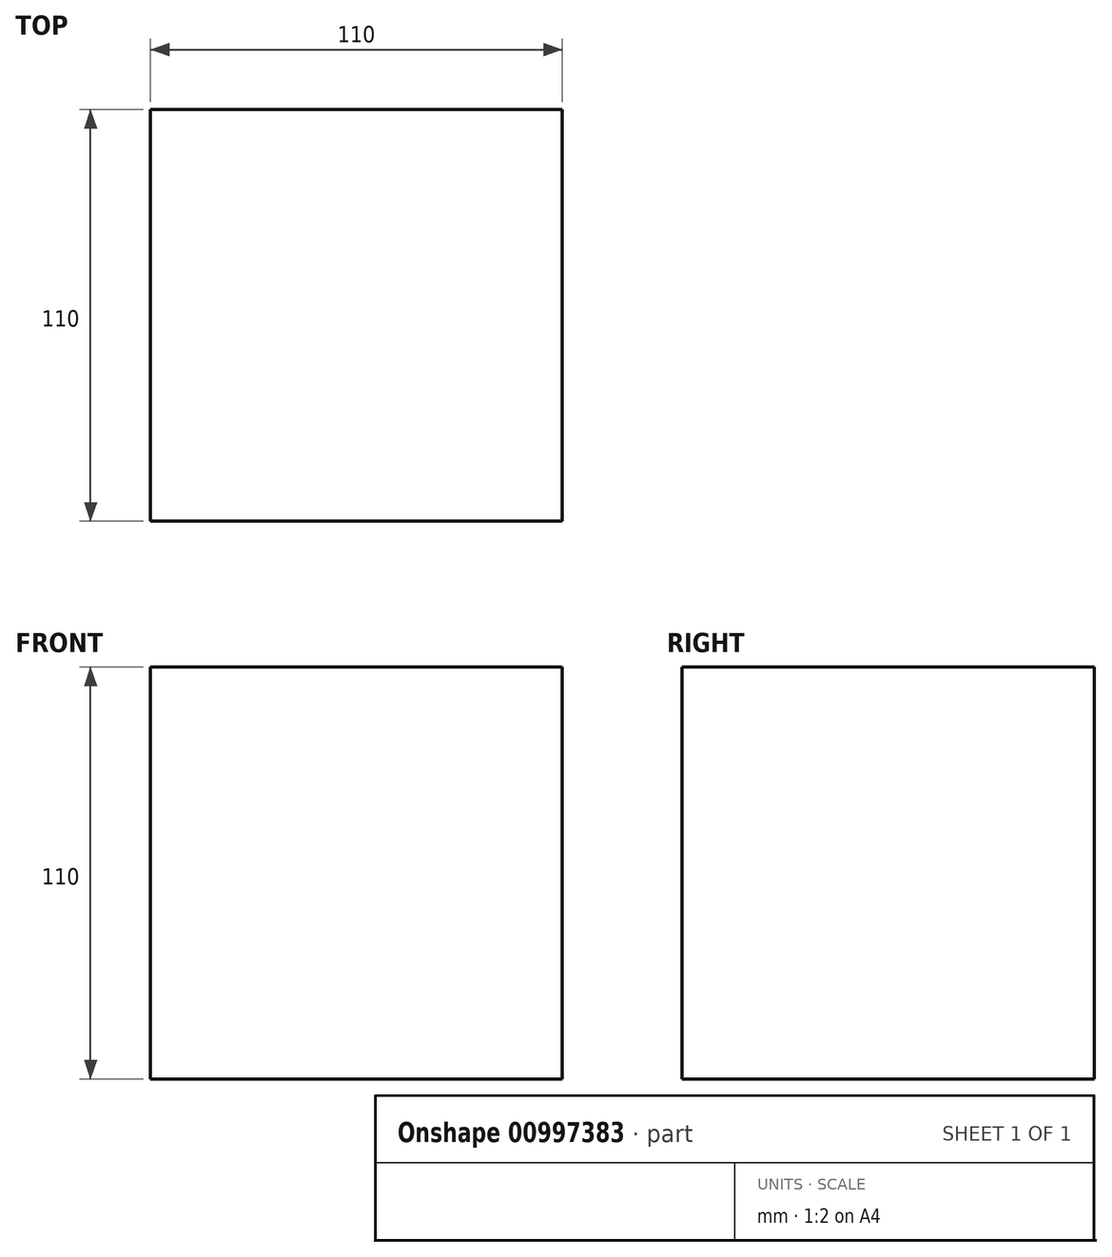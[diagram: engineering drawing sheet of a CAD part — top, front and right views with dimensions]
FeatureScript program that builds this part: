
annotation { "Feature Type Name" : "Feature", "Feature Type Description" : "" }
export const myFeature = defineFeature(function(context is Context, id is Id, definition is map)
    precondition{}
    {
        {
            var Q0;
            Q0=qCreatedBy(makeId("Front.planeOp"),FACE);
            var sketch = newSketch(context, id + "F0", { "sketchPlane" : qUnion([Q0])});
            skLineSegment(sketch, "E0.bottom", {"start": v(55, 55) * mm, "end": v(-55, 55) * mm});
            skLineSegment(sketch, "E0.top", {"start": v(55, -55) * mm, "end": v(-55, -55) * mm});
            skLineSegment(sketch, "E0.left", {"start": v(55, 55) * mm, "end": v(55, -55) * mm});
            skLineSegment(sketch, "E0.right", {"start": v(-55, 55) * mm, "end": v(-55, -55) * mm});
            skPoint(sketch, "E0.middle", {"position": v(0, 0) * mm});
            skSolve(sketch);
        }
        {
            var Q0;
            Q0 = qSketchRegion(id + "F0", true);
            var Q1;
            Q1=makeQuery(id+"F0.imprint","IMPRINT",FACE,{"disambiguationData":[TD([[makeQuery(id+"F0.imprint","IMPRINT",EDGE,{"derivedFrom":sQuery(id+"F0.wireOp",EDGE,"E0.bottom")}),1.0]])]});
            extrude(context, id + "F1", {"entities" : qUnion([Q0, Q1]), "depth" : 110 * mm, "offsetDistance" : 25 * mm});
        }
    });
